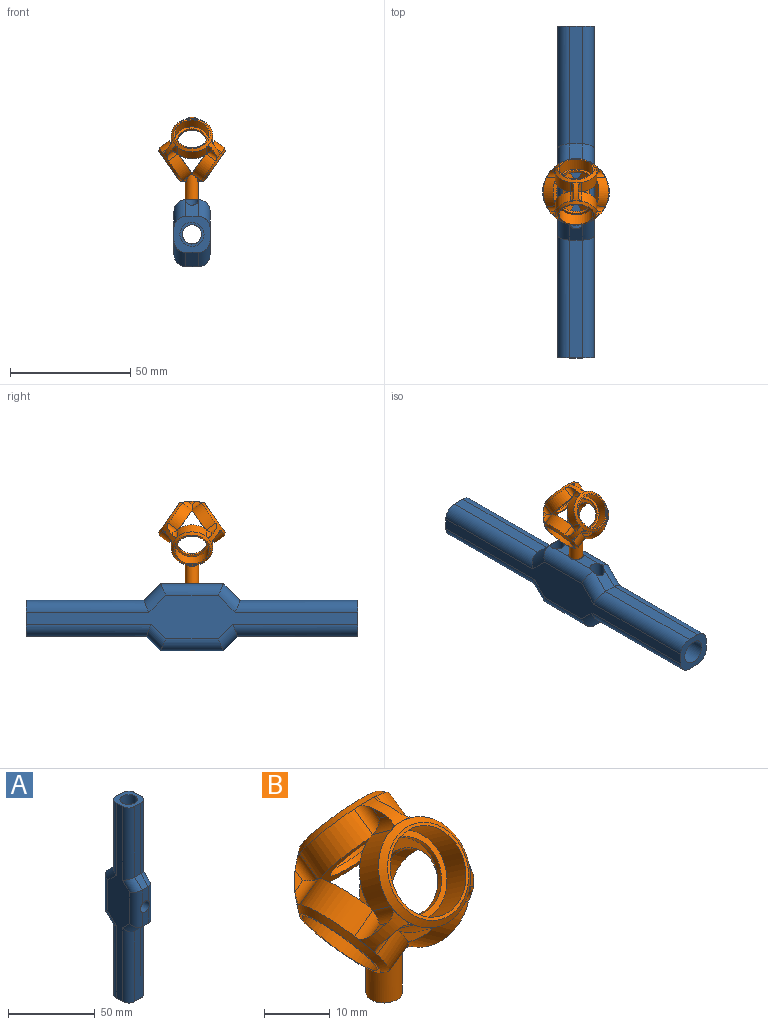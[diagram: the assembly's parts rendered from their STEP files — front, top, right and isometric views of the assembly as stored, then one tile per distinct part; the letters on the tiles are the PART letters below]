
ASSEMBLY  parts=2 mates=1
PART A: 58 faces, bbox 15x28x138 mm
  f0: cylinder r=5mm len=51mm, axis (0,0,-1), area 1602.2mm2, adj f20,f57
  f1: plane 10.21x5mm, normal (0,-1,0), area 47.8mm2, adj f13,f32,f38,f49
  f2: plane 0.29x0.22mm, normal (0,1,0), area 0mm2, adj f8,f34,f43
  f3: plane 7.75x5mm, normal (0,1,0), area 29.3mm2, adj f8,f10,f43,f54
  f4: plane 9.09x5mm, normal (0,1,0), area 36mm2, adj f9,f10,f43,f54
  f5: cylinder r=6mm len=22mm, axis (0,0,-1), area 808.8mm2, adj f8,f9,f18,f23
  f6: plane 138x18mm, normal (-1,0,0), area 1059.2mm2, adj f28,f31,f36,f37,f38,f39,f40,f41
  f7: plane 138x18mm, normal (1,0,0), area 1059.2mm2, adj f28,f31,f46,f47,f48,f49,f50,f51
  f8: cylinder r=3mm len=9.3mm, axis (0,-1,0), area 164.1mm2, adj f2,f3,f5,f11,f16,f34,f43,f54
  f9: cylinder r=3mm len=9.3mm, axis (0,-1,0), area 155mm2, adj f4,f5,f21,f35,f42,f43,f52,f54
  f10: cylinder r=2.99mm len=7mm, axis (0,-1,0), area 131.7mm2, adj f3,f4,f12,f43,f54
  f11: plane 0.29x0.22mm, normal (0,1,0), area 0mm2, adj f8,f34,f54
  f12: plane 5.99x5.99mm, normal (0,1,0), area 28.2mm2, adj f10
  f13: cylinder r=3.75mm len=7.5mm, axis (0,1,0), area 140.3mm2, adj f1,f14,f15,f38,f49
  f14: plane 10.21x5mm, normal (0,-1,0), area 47.8mm2, adj f13,f33,f38,f49
  f15: plane 7.5x7.5mm, normal (0,-1,0), area 44.2mm2, adj f13
  f16: cylinder r=6mm len=6mm, axis (0,0,-1), area 14.9mm2, adj f8,f18
  f17: cylinder r=5mm len=10mm, axis (0,0,-1), area 125.7mm2, adj f31,f56
  f18: plane 12x12mm, normal (0,0,1), area 62.8mm2, adj f5,f16,f19
  f19: cylinder r=4mm len=8mm, axis (0,0,1), area 50.3mm2, adj f18,f20
  f20: plane 10x10mm, normal (0,0,-1), area 28.3mm2, adj f0,f19
  f21: cylinder r=6mm len=6mm, axis (0,0,-1), area 23mm2, adj f9,f23
  f22: cylinder r=5mm len=56mm, axis (0,0,-1), area 1759.3mm2, adj f25,f28
  f23: plane 12x12mm, normal (0,0,-1), area 62.8mm2, adj f5,f21,f24
  f24: cylinder r=4mm len=8mm, axis (0,0,-1), area 50.3mm2, adj f23,f25
  f25: plane 10x10mm, normal (0,0,1), area 28.3mm2, adj f22,f24
  f26: plane 49x5mm, normal (0,1,0), area 245mm2, adj f28,f35,f41,f51
  f27: plane 50x5mm, normal (0,-1,0), area 250mm2, adj f28,f32,f39,f48
  f28: plane 15x15mm, normal (0,0,1), area 125mm2, adj f6,f7,f22,f26,f27,f39,f41,f48
  f29: plane 50x5mm, normal (0,-1,0), area 250mm2, adj f31,f33,f36,f46
  f30: plane 49x5mm, normal (0,1,0), area 245mm2, adj f31,f34,f44,f53
  f31: plane 15x15mm, normal (0,0,-1), area 125mm2, adj f6,f7,f17,f29,f30,f36,f44,f46
  f32: plane 6x6mm, normal (0,-0.71,0.71), area 42.4mm2, adj f1,f27,f40,f50
  f33: plane 6x6mm, normal (0,-0.71,-0.71), area 42.4mm2, adj f14,f29,f37,f47
  f34: plane 7x7mm, normal (0,0.71,-0.71), area 44.8mm2, adj f2,f8,f11,f30,f45,f55
  f35: plane 5.95x5.95mm, normal (0,0.71,0.71), area 35.4mm2, adj f9,f26,f42,f52
  f36: cylinder r=5mm len=52.07mm, axis (0,0,-1), area 398.6mm2, adj f6,f29,f31,f37
  f37: cylinder r=5mm len=11mm, axis (0,0.71,-0.71), area 66.6mm2, adj f6,f33,f36,f38
  f38: cylinder r=5mm len=26mm, axis (0,0,1), area 187.5mm2, adj f1,f6,f13,f14,f37,f40
  f39: cylinder r=5mm len=52.07mm, axis (0,0,-1), area 398.6mm2, adj f6,f27,f28,f40
  f40: cylinder r=5mm len=11mm, axis (0,0.71,0.71), area 66.6mm2, adj f6,f32,f38,f39
  f41: cylinder r=5mm len=51.07mm, axis (0,0,1), area 390.8mm2, adj f6,f26,f28,f42
  f42: cylinder r=5mm len=11.99mm, axis (0,-0.71,0.71), area 77.4mm2, adj f6,f9,f35,f41,f43
  f43: cylinder r=5mm len=25.99mm, axis (0,0,-1), area 189.3mm2, adj f2,f3,f4,f6,f8,f9,f10,f42
  f44: cylinder r=5mm len=51.07mm, axis (0,0,1), area 390.8mm2, adj f6,f30,f31,f45
  f45: cylinder r=5mm len=12mm, axis (0,-0.71,-0.71), area 77.8mm2, adj f6,f34,f43,f44
  f46: cylinder r=5mm len=52.07mm, axis (0,0,1), area 398.6mm2, adj f7,f29,f31,f47
  f47: cylinder r=5mm len=11mm, axis (0,0.71,-0.71), area 66.6mm2, adj f7,f33,f46,f49
  f48: cylinder r=5mm len=52.07mm, axis (0,0,1), area 398.6mm2, adj f7,f27,f28,f50
  f49: cylinder r=5mm len=26mm, axis (0,0,-1), area 187.5mm2, adj f1,f7,f13,f14,f47,f50
  f50: cylinder r=5mm len=11mm, axis (0,0.71,0.71), area 66.6mm2, adj f7,f32,f48,f49
  f51: cylinder r=5mm len=51.07mm, axis (0,0,-1), area 390.8mm2, adj f7,f26,f28,f52
  f52: cylinder r=5mm len=11.99mm, axis (0,-0.71,0.71), area 77.4mm2, adj f7,f9,f35,f51,f54
  f53: cylinder r=5mm len=51.07mm, axis (0,0,-1), area 390.8mm2, adj f7,f30,f31,f55
  f54: cylinder r=5mm len=25.99mm, axis (0,0,1), area 189.3mm2, adj f3,f4,f7,f8,f9,f10,f11,f52
  f55: cylinder r=5mm len=12mm, axis (0,-0.71,-0.71), area 77.8mm2, adj f7,f34,f53,f54
  f56: plane 10x10mm, normal (0,0,-1), area 28.3mm2, adj f17,f57
  f57: cone r=7mm half-angle=45deg, axis (0,0,1), area 40mm2, adj f0,f56
PART B: 104 faces, bbox 27.7x27.7x35 mm
  f0: plane 17.1x13.47mm, normal (-0.82,0,0.58), area 103.3mm2, adj f1,f2,f10,f40,f64,f65,f66,f103
  f1: cylinder r=6.05mm len=12.1mm, axis (0.82,0,-0.58), area 37.9mm2, adj f0,f5,f103
  f2: plane 17.1x13.47mm, normal (0.82,0,0.58), area 103.3mm2, adj f0,f3,f10,f40,f83,f84,f85,f103
  f3: cylinder r=6.05mm len=12.1mm, axis (-0.82,0,-0.58), area 37.9mm2, adj f2,f4,f103
  f4: plane 14.1x11.51mm, normal (-0.82,0,-0.58), area 41.2mm2, adj f3,f86
  f5: plane 14.1x11.51mm, normal (0.82,0,-0.58), area 41.2mm2, adj f1,f67
  f6: cylinder r=13.64mm len=3.51mm, axis (0,1,0), area 3.1mm2, adj f69,f70,f81,f82,f102
  f7: cylinder r=8.55mm len=11.77mm, axis (0,0.82,-0.58), area 64.8mm2, adj f10,f30,f32,f33,f66,f84
  f8: cylinder r=8.55mm len=11.21mm, axis (0,0.82,-0.58), area 64.8mm2, adj f10,f30,f31,f36,f39,f83
  f9: cylinder r=8.55mm len=11.21mm, axis (0,0.82,-0.58), area 64.8mm2, adj f10,f30,f34,f35,f38,f64
  f10: plane 17.1x13.47mm, normal (0,0.82,-0.58), area 107.1mm2, adj f0,f2,f7,f8,f9,f14,f40
  f11: cylinder r=7.05mm len=14.4mm, axis (0,0.82,-0.58), area 221.5mm2, adj f12,f13
  f12: plane 15.1x12.33mm, normal (0,-0.82,0.58), area 22.9mm2, adj f11,f30
  f13: plane 14.1x11.51mm, normal (0,-0.82,0.58), area 41.2mm2, adj f11,f14
  f14: cylinder r=6.05mm len=12.1mm, axis (0,-0.82,0.58), area 38mm2, adj f10,f13
  f15: plane 2.43x0.29mm, normal (0,-0.82,0.58), area 0.1mm2, adj f19,f30,f35
  f16: plane 3.25x1.25mm, normal (1,0,0), area 2.1mm2, adj f19,f35,f63
  f17: plane 3.25x1.25mm, normal (-1,0,0), area 2.1mm2, adj f19,f36,f62
  f18: plane 2.43x0.29mm, normal (0,-0.82,0.58), area 0.1mm2, adj f19,f30,f36
  f19: cylinder r=13.64mm len=7.47mm, axis (-1,0,0), area 17mm2, adj f15,f16,f17,f18,f35,f36,f45,f46
  f20: plane 2.3x1.63mm, normal (-0.5,-0.5,-0.71), area 2.1mm2, adj f24,f33,f80
  f21: plane 2.3x1.63mm, normal (0.5,0.5,0.71), area 2.1mm2, adj f24,f34,f79
  f22: plane 1.58x1.52mm, normal (0,-0.82,0.58), area 0.1mm2, adj f24,f30,f33
  f23: plane 1.86x1.32mm, normal (0,-0.82,0.58), area 0.1mm2, adj f24,f30,f34
  f24: cylinder r=13.64mm len=7.76mm, axis (0.5,0.5,0.71), area 17mm2, adj f20,f21,f22,f23,f33,f34,f72,f73
  f25: plane 2.3x1.63mm, normal (-0.5,0.5,0.71), area 2.1mm2, adj f29,f31,f96
  f26: plane 2.3x1.63mm, normal (0.5,-0.5,-0.71), area 2.1mm2, adj f29,f32,f95
  f27: plane 1.86x1.32mm, normal (0,-0.82,0.58), area 0.1mm2, adj f29,f30,f31
  f28: plane 1.58x1.52mm, normal (0,-0.82,0.58), area 0.1mm2, adj f29,f30,f32
  f29: cylinder r=13.64mm len=7.76mm, axis (0.5,-0.5,-0.71), area 17mm2, adj f25,f26,f27,f28,f31,f32,f92,f93
  f30: cone r=7.55mm half-angle=45deg, axis (0,0.82,-0.58), area 71.5mm2, adj f7,f8,f9,f12,f15,f18,f22,f23
  f31: cylinder r=2mm len=5.21mm, axis (0,0.82,-0.58), area 9.8mm2, adj f8,f25,f27,f29,f96
  f32: cylinder r=2mm len=4.26mm, axis (0,0.82,-0.58), area 9.8mm2, adj f7,f26,f28,f29,f95
  f33: cylinder r=2mm len=4.26mm, axis (0,0.82,-0.58), area 9.8mm2, adj f7,f20,f22,f24,f80
  f34: cylinder r=2mm len=5.21mm, axis (0,0.82,-0.58), area 9.8mm2, adj f9,f21,f23,f24,f79
  f35: cylinder r=2mm len=5.05mm, axis (0,0.82,-0.58), area 9.8mm2, adj f9,f15,f16,f19,f63
  f36: cylinder r=2mm len=5.05mm, axis (0,0.82,-0.58), area 9.8mm2, adj f8,f17,f18,f19,f62
  f37: cylinder r=8.55mm len=11.77mm, axis (0,-0.82,-0.58), area 64.8mm2, adj f40,f57,f59,f60,f65,f85
  f38: cylinder r=8.55mm len=11.21mm, axis (0,-0.82,-0.58), area 64.8mm2, adj f9,f40,f57,f58,f63,f64
  f39: cylinder r=8.55mm len=11.21mm, axis (0,-0.82,-0.58), area 64.8mm2, adj f8,f40,f57,f61,f62,f83
  f40: plane 17.1x13.47mm, normal (0,-0.82,-0.58), area 107.1mm2, adj f0,f2,f10,f37,f38,f39,f44
  f41: cylinder r=7.05mm len=14.4mm, axis (0,-0.82,-0.58), area 221.5mm2, adj f42,f43
  f42: plane 15.1x12.33mm, normal (0,0.82,0.58), area 22.9mm2, adj f41,f57
  f43: plane 14.1x11.51mm, normal (0,0.82,0.58), area 41.2mm2, adj f41,f44
  f44: cylinder r=6.05mm len=12.1mm, axis (0,0.82,0.58), area 38mm2, adj f40,f43
  f45: plane 2.43x0.29mm, normal (0,0.82,0.58), area 0.1mm2, adj f19,f57,f62
  f46: plane 2.43x0.29mm, normal (0,0.82,0.58), area 0.1mm2, adj f19,f57,f63
  f47: plane 2.3x1.63mm, normal (0.5,0.5,-0.71), area 2.1mm2, adj f51,f60,f98
  f48: plane 2.3x1.63mm, normal (-0.5,-0.5,0.71), area 2.1mm2, adj f51,f61,f97
  f49: plane 1.58x1.52mm, normal (0,0.82,0.58), area 0.1mm2, adj f51,f57,f60
  f50: plane 1.86x1.32mm, normal (0,0.82,0.58), area 0.1mm2, adj f51,f57,f61
  f51: cylinder r=13.64mm len=7.76mm, axis (-0.5,-0.5,0.71), area 17mm2, adj f47,f48,f49,f50,f60,f61,f90,f91
  f52: plane 2.3x1.63mm, normal (0.5,-0.5,0.71), area 2.1mm2, adj f56,f58,f78
  f53: plane 2.3x1.63mm, normal (-0.5,0.5,-0.71), area 2.1mm2, adj f56,f59,f77
  f54: plane 1.86x1.32mm, normal (0,0.82,0.58), area 0.1mm2, adj f56,f57,f58
  f55: plane 1.58x1.52mm, normal (0,0.82,0.58), area 0.1mm2, adj f56,f57,f59
  f56: cylinder r=13.64mm len=7.76mm, axis (-0.5,0.5,-0.71), area 17mm2, adj f52,f53,f54,f55,f58,f59,f74,f75
  f57: cone r=7.55mm half-angle=45deg, axis (0,-0.82,-0.58), area 71.5mm2, adj f37,f38,f39,f42,f45,f46,f49,f50
  f58: cylinder r=2mm len=5.21mm, axis (0,-0.82,-0.58), area 9.8mm2, adj f38,f52,f54,f56,f78
  f59: cylinder r=2mm len=4.26mm, axis (0,-0.82,-0.58), area 9.8mm2, adj f37,f53,f55,f56,f77
  f60: cylinder r=2mm len=4.26mm, axis (0,-0.82,-0.58), area 9.8mm2, adj f37,f47,f49,f51,f98
  f61: cylinder r=2mm len=5.21mm, axis (0,-0.82,-0.58), area 9.8mm2, adj f39,f48,f50,f51,f97
  f62: cylinder r=2mm len=5.05mm, axis (0,-0.82,-0.58), area 9.8mm2, adj f17,f19,f36,f39,f45
  f63: cylinder r=2mm len=5.05mm, axis (0,-0.82,-0.58), area 9.8mm2, adj f16,f19,f35,f38,f46
  f64: cylinder r=8.55mm len=11.77mm, axis (-0.82,0,0.58), area 64.8mm2, adj f0,f9,f38,f76,f78,f79
  f65: cylinder r=8.55mm len=11.21mm, axis (-0.82,0,0.58), area 64.4mm2, adj f0,f37,f76,f77,f82,f85,f102
  f66: cylinder r=8.55mm len=11.21mm, axis (-0.82,0,0.58), area 64.4mm2, adj f0,f7,f76,f80,f81,f84,f102
  f67: cylinder r=7.05mm len=14.4mm, axis (-0.82,0,0.58), area 221.5mm2, adj f5,f68
  f68: plane 15.1x12.33mm, normal (0.82,0,-0.58), area 22.9mm2, adj f67,f76
  f69: plane 2.43x0.29mm, normal (0.82,0,-0.58), area 0.1mm2, adj f6,f76,f81
  f70: plane 2.43x0.29mm, normal (0.82,0,-0.58), area 0.1mm2, adj f6,f76,f82
  f71: cylinder r=13.64mm len=3.51mm, axis (0,1,0), area 3mm2, adj f88,f89,f99,f100,f102
  f72: plane 1.58x1.52mm, normal (0.82,0,-0.58), area 0.1mm2, adj f24,f76,f79
  f73: plane 1.86x1.32mm, normal (0.82,0,-0.58), area 0.1mm2, adj f24,f76,f80
  f74: plane 1.86x1.32mm, normal (0.82,0,-0.58), area 0.1mm2, adj f56,f76,f77
  f75: plane 1.58x1.52mm, normal (0.82,0,-0.58), area 0.1mm2, adj f56,f76,f78
  f76: cone r=7.55mm half-angle=45deg, axis (-0.82,0,0.58), area 71.5mm2, adj f64,f65,f66,f68,f69,f70,f72,f73
  f77: cylinder r=2mm len=5.21mm, axis (-0.82,0,0.58), area 9.8mm2, adj f53,f56,f59,f65,f74
  f78: cylinder r=2mm len=4.26mm, axis (-0.82,0,0.58), area 9.8mm2, adj f52,f56,f58,f64,f75
  f79: cylinder r=2mm len=4.26mm, axis (-0.82,0,0.58), area 9.8mm2, adj f21,f24,f34,f64,f72
  f80: cylinder r=2mm len=5.21mm, axis (-0.82,0,0.58), area 9.8mm2, adj f20,f24,f33,f66,f73
  f81: cylinder r=2mm len=3.4mm, axis (-0.82,0,0.58), area 3.1mm2, adj f6,f66,f69,f102
  f82: cylinder r=2mm len=3.4mm, axis (-0.82,0,0.58), area 3.1mm2, adj f6,f65,f70,f102
  f83: cylinder r=8.55mm len=11.77mm, axis (0.82,0,0.58), area 64.8mm2, adj f2,f8,f39,f94,f96,f97
  f84: cylinder r=8.55mm len=11.21mm, axis (0.82,0,0.58), area 64.4mm2, adj f2,f7,f66,f94,f95,f100,f102
  f85: cylinder r=8.55mm len=11.21mm, axis (0.82,0,0.58), area 64.4mm2, adj f2,f37,f65,f94,f98,f99,f102
  f86: cylinder r=7.05mm len=14.4mm, axis (0.82,0,0.58), area 221.5mm2, adj f4,f87
  f87: plane 15.1x12.33mm, normal (-0.82,0,-0.58), area 22.9mm2, adj f86,f94
  f88: plane 2.43x0.29mm, normal (-0.82,0,-0.58), area 0.1mm2, adj f71,f94,f99
  f89: plane 2.43x0.29mm, normal (-0.82,0,-0.58), area 0.1mm2, adj f71,f94,f100
  f90: plane 1.58x1.52mm, normal (-0.82,0,-0.58), area 0.1mm2, adj f51,f94,f97
  f91: plane 1.86x1.32mm, normal (-0.82,0,-0.58), area 0.1mm2, adj f51,f94,f98
  f92: plane 1.86x1.32mm, normal (-0.82,0,-0.58), area 0.1mm2, adj f29,f94,f95
  f93: plane 1.58x1.52mm, normal (-0.82,0,-0.58), area 0.1mm2, adj f29,f94,f96
  f94: cone r=7.55mm half-angle=45deg, axis (0.82,0,0.58), area 71.5mm2, adj f83,f84,f85,f87,f88,f89,f90,f91
  f95: cylinder r=2mm len=5.21mm, axis (0.82,0,0.58), area 9.8mm2, adj f26,f29,f32,f84,f92
  f96: cylinder r=2mm len=4.26mm, axis (0.82,0,0.58), area 9.8mm2, adj f25,f29,f31,f83,f93
  f97: cylinder r=2mm len=4.26mm, axis (0.82,0,0.58), area 9.8mm2, adj f48,f51,f61,f83,f90
  f98: cylinder r=2mm len=5.21mm, axis (0.82,0,0.58), area 9.8mm2, adj f47,f51,f60,f85,f91
  f99: cylinder r=2mm len=3.4mm, axis (0.82,0,0.58), area 3.1mm2, adj f71,f85,f88,f102
  f100: cylinder r=2mm len=3.4mm, axis (0.82,0,0.58), area 3.1mm2, adj f71,f84,f89,f102
  f101: plane 5.5x5.5mm, normal (0,0,-1), area 19.2mm2, adj f102,f103
  f102: cylinder r=2.75mm len=10.71mm, axis (0,0,1), area 151.8mm2, adj f6,f65,f66,f71,f81,f82,f84,f85
  f103: cylinder r=1.2mm len=12.45mm, axis (0,0,-1), area 89.9mm2, adj f0,f1,f2,f3,f101
PLACE A rot(axis=(1,0,0),90deg) t=(21.08,0.82,-41.16)mm
PLACE B t=(21.08,0.82,-13.54)mm
MATE fastened A.f10 <-> B.f102  axis (0,0,1) through (21.08,0.82,-34.16)mm
